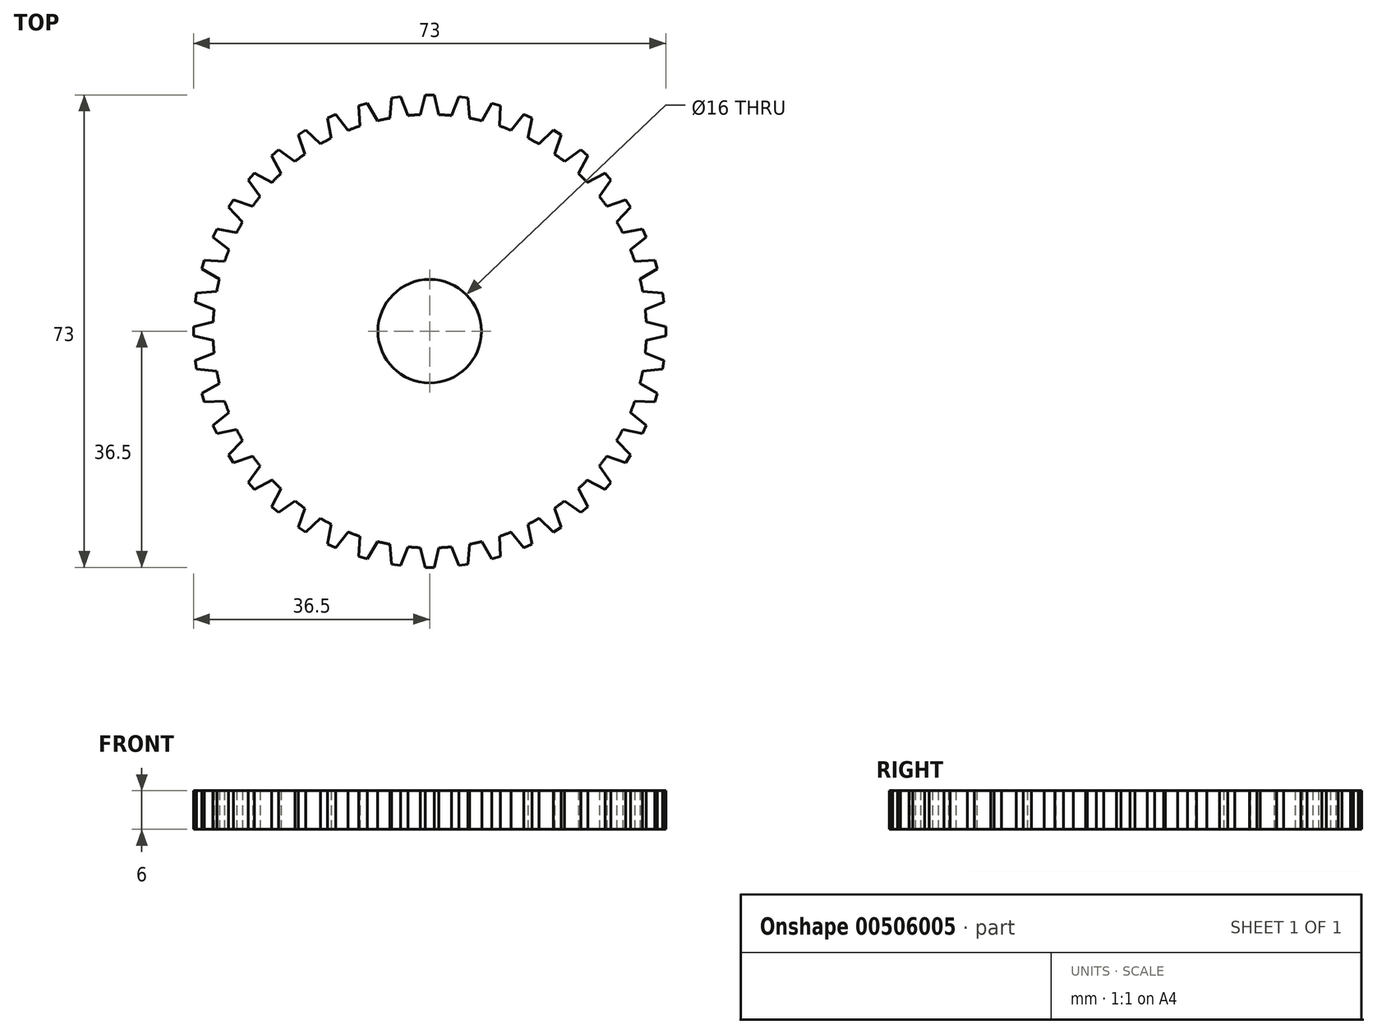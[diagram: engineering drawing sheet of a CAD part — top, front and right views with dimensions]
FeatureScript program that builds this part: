
annotation { "Feature Type Name" : "Feature", "Feature Type Description" : "" }
export const myFeature = defineFeature(function(context is Context, id is Id, definition is map)
    precondition{}
    {
        {
            var Q0;
            Q0=qCreatedBy(makeId("Top.planeOp"),FACE);
            var sketch = newSketch(context, id + "F0", { "sketchPlane" : qUnion([Q0])});
            skPoint(sketch, "E0.center", {"position": v(0, 0) * mm});
            skCircle(sketch, "E1", {"center": v(0, 0) * mm, "radius": 33.5 * mm});
            skLineSegment(sketch, "E2", {"start": v(0, 36.5) * mm, "end": v(0.7, 36.5) * mm});
            skLineSegment(sketch, "E3", {"start": v(0.7, 36.5) * mm, "end": v(1.43, 33.47) * mm});
            skLineSegment(sketch, "E4.MirrorCS", {"start": v(0, 36.5) * mm, "end": v(-0.7, 36.5) * mm});
            skLineSegment(sketch, "E5.MirrorCS", {"start": v(-0.7, 36.5) * mm, "end": v(-1.43, 33.47) * mm});
            skLineSegment(sketch, "E6.1.0", {"start": v(-5.2, 36.13) * mm, "end": v(-4.5, 36.23) * mm});
            skLineSegment(sketch, "E6.1.1", {"start": v(-4.5, 36.23) * mm, "end": v(-3.35, 33.33) * mm});
            skLineSegment(sketch, "E6.1.2", {"start": v(-5.89, 36.03) * mm, "end": v(-6.18, 32.93) * mm});
            skLineSegment(sketch, "E6.1.3", {"start": v(-5.2, 36.13) * mm, "end": v(-5.89, 36.03) * mm});
            skLineSegment(sketch, "E6.2.0", {"start": v(-10.28, 35.02) * mm, "end": v(-9.61, 35.22) * mm});
            skLineSegment(sketch, "E6.2.1", {"start": v(-9.61, 35.22) * mm, "end": v(-8.06, 32.52) * mm});
            skLineSegment(sketch, "E6.2.2", {"start": v(-10.95, 34.82) * mm, "end": v(-10.8, 31.71) * mm});
            skLineSegment(sketch, "E6.2.3", {"start": v(-10.28, 35.02) * mm, "end": v(-10.95, 34.82) * mm});
            skLineSegment(sketch, "E6.3.0", {"start": v(-15.16, 33.2) * mm, "end": v(-14.53, 33.5) * mm});
            skLineSegment(sketch, "E6.3.1", {"start": v(-14.53, 33.5) * mm, "end": v(-12.6, 31.04) * mm});
            skLineSegment(sketch, "E6.3.2", {"start": v(-15.8, 32.91) * mm, "end": v(-15.2, 29.85) * mm});
            skLineSegment(sketch, "E6.3.3", {"start": v(-15.16, 33.2) * mm, "end": v(-15.8, 32.91) * mm});
            skLineSegment(sketch, "E6.4.0", {"start": v(-19.73, 30.7) * mm, "end": v(-19.14, 31.08) * mm});
            skLineSegment(sketch, "E6.4.1", {"start": v(-19.14, 31.08) * mm, "end": v(-16.9, 28.93) * mm});
            skLineSegment(sketch, "E6.4.2", {"start": v(-20.32, 30.33) * mm, "end": v(-19.3, 27.38) * mm});
            skLineSegment(sketch, "E6.4.3", {"start": v(-19.73, 30.7) * mm, "end": v(-20.32, 30.33) * mm});
            skLineSegment(sketch, "E6.5.0", {"start": v(-23.9, 27.58) * mm, "end": v(-23.37, 28.04) * mm});
            skLineSegment(sketch, "E6.5.1", {"start": v(-23.37, 28.04) * mm, "end": v(-20.84, 26.23) * mm});
            skLineSegment(sketch, "E6.5.2", {"start": v(-24.43, 27.13) * mm, "end": v(-23, 24.36) * mm});
            skLineSegment(sketch, "E6.5.3", {"start": v(-23.9, 27.58) * mm, "end": v(-24.43, 27.13) * mm});
            skLineSegment(sketch, "E6.6.0", {"start": v(-27.58, 23.9) * mm, "end": v(-27.13, 24.43) * mm});
            skLineSegment(sketch, "E6.6.1", {"start": v(-27.13, 24.43) * mm, "end": v(-24.36, 23) * mm});
            skLineSegment(sketch, "E6.6.2", {"start": v(-28.04, 23.37) * mm, "end": v(-26.23, 20.84) * mm});
            skLineSegment(sketch, "E6.6.3", {"start": v(-27.58, 23.9) * mm, "end": v(-28.04, 23.37) * mm});
            skLineSegment(sketch, "E6.7.0", {"start": v(-30.7, 19.73) * mm, "end": v(-30.33, 20.32) * mm});
            skLineSegment(sketch, "E6.7.1", {"start": v(-30.33, 20.32) * mm, "end": v(-27.38, 19.3) * mm});
            skLineSegment(sketch, "E6.7.2", {"start": v(-31.08, 19.14) * mm, "end": v(-28.93, 16.9) * mm});
            skLineSegment(sketch, "E6.7.3", {"start": v(-30.7, 19.73) * mm, "end": v(-31.08, 19.14) * mm});
            skLineSegment(sketch, "E6.8.0", {"start": v(-33.2, 15.16) * mm, "end": v(-32.91, 15.8) * mm});
            skLineSegment(sketch, "E6.8.1", {"start": v(-32.91, 15.8) * mm, "end": v(-29.85, 15.2) * mm});
            skLineSegment(sketch, "E6.8.2", {"start": v(-33.5, 14.53) * mm, "end": v(-31.04, 12.6) * mm});
            skLineSegment(sketch, "E6.8.3", {"start": v(-33.2, 15.16) * mm, "end": v(-33.5, 14.53) * mm});
            skLineSegment(sketch, "E6.9.0", {"start": v(-35.02, 10.28) * mm, "end": v(-34.82, 10.95) * mm});
            skLineSegment(sketch, "E6.9.1", {"start": v(-34.82, 10.95) * mm, "end": v(-31.71, 10.8) * mm});
            skLineSegment(sketch, "E6.9.2", {"start": v(-35.22, 9.61) * mm, "end": v(-32.52, 8.06) * mm});
            skLineSegment(sketch, "E6.9.3", {"start": v(-35.02, 10.28) * mm, "end": v(-35.22, 9.61) * mm});
            skLineSegment(sketch, "E6.10.0", {"start": v(-36.13, 5.2) * mm, "end": v(-36.03, 5.89) * mm});
            skLineSegment(sketch, "E6.10.1", {"start": v(-36.03, 5.89) * mm, "end": v(-32.93, 6.18) * mm});
            skLineSegment(sketch, "E6.10.2", {"start": v(-36.23, 4.5) * mm, "end": v(-33.33, 3.35) * mm});
            skLineSegment(sketch, "E6.10.3", {"start": v(-36.13, 5.2) * mm, "end": v(-36.23, 4.5) * mm});
            skLineSegment(sketch, "E6.11.0", {"start": v(-36.5, 0) * mm, "end": v(-36.5, 0.7) * mm});
            skLineSegment(sketch, "E6.11.1", {"start": v(-36.5, 0.7) * mm, "end": v(-33.47, 1.43) * mm});
            skLineSegment(sketch, "E6.11.2", {"start": v(-36.5, -0.7) * mm, "end": v(-33.47, -1.43) * mm});
            skLineSegment(sketch, "E6.11.3", {"start": v(-36.5, 0) * mm, "end": v(-36.5, -0.7) * mm});
            skLineSegment(sketch, "E6.12.0", {"start": v(-36.13, -5.2) * mm, "end": v(-36.23, -4.5) * mm});
            skLineSegment(sketch, "E6.12.1", {"start": v(-36.23, -4.5) * mm, "end": v(-33.33, -3.35) * mm});
            skLineSegment(sketch, "E6.12.2", {"start": v(-36.03, -5.89) * mm, "end": v(-32.93, -6.18) * mm});
            skLineSegment(sketch, "E6.12.3", {"start": v(-36.13, -5.2) * mm, "end": v(-36.03, -5.89) * mm});
            skLineSegment(sketch, "E6.13.0", {"start": v(-35.02, -10.28) * mm, "end": v(-35.22, -9.61) * mm});
            skLineSegment(sketch, "E6.13.1", {"start": v(-35.22, -9.61) * mm, "end": v(-32.52, -8.06) * mm});
            skLineSegment(sketch, "E6.13.2", {"start": v(-34.82, -10.95) * mm, "end": v(-31.71, -10.8) * mm});
            skLineSegment(sketch, "E6.13.3", {"start": v(-35.02, -10.28) * mm, "end": v(-34.82, -10.95) * mm});
            skLineSegment(sketch, "E6.14.0", {"start": v(-33.2, -15.16) * mm, "end": v(-33.5, -14.53) * mm});
            skLineSegment(sketch, "E6.14.1", {"start": v(-33.5, -14.53) * mm, "end": v(-31.04, -12.6) * mm});
            skLineSegment(sketch, "E6.14.2", {"start": v(-32.91, -15.8) * mm, "end": v(-29.85, -15.2) * mm});
            skLineSegment(sketch, "E6.14.3", {"start": v(-33.2, -15.16) * mm, "end": v(-32.91, -15.8) * mm});
            skLineSegment(sketch, "E6.15.0", {"start": v(-30.7, -19.73) * mm, "end": v(-31.08, -19.14) * mm});
            skLineSegment(sketch, "E6.15.1", {"start": v(-31.08, -19.14) * mm, "end": v(-28.93, -16.9) * mm});
            skLineSegment(sketch, "E6.15.2", {"start": v(-30.33, -20.32) * mm, "end": v(-27.38, -19.3) * mm});
            skLineSegment(sketch, "E6.15.3", {"start": v(-30.7, -19.73) * mm, "end": v(-30.33, -20.32) * mm});
            skLineSegment(sketch, "E6.16.0", {"start": v(-27.58, -23.9) * mm, "end": v(-28.04, -23.37) * mm});
            skLineSegment(sketch, "E6.16.1", {"start": v(-28.04, -23.37) * mm, "end": v(-26.23, -20.84) * mm});
            skLineSegment(sketch, "E6.16.2", {"start": v(-27.13, -24.43) * mm, "end": v(-24.36, -23) * mm});
            skLineSegment(sketch, "E6.16.3", {"start": v(-27.58, -23.9) * mm, "end": v(-27.13, -24.43) * mm});
            skLineSegment(sketch, "E6.17.0", {"start": v(-23.9, -27.58) * mm, "end": v(-24.43, -27.13) * mm});
            skLineSegment(sketch, "E6.17.1", {"start": v(-24.43, -27.13) * mm, "end": v(-23, -24.36) * mm});
            skLineSegment(sketch, "E6.17.2", {"start": v(-23.37, -28.04) * mm, "end": v(-20.84, -26.23) * mm});
            skLineSegment(sketch, "E6.17.3", {"start": v(-23.9, -27.58) * mm, "end": v(-23.37, -28.04) * mm});
            skLineSegment(sketch, "E6.18.0", {"start": v(-19.73, -30.7) * mm, "end": v(-20.32, -30.33) * mm});
            skLineSegment(sketch, "E6.18.1", {"start": v(-20.32, -30.33) * mm, "end": v(-19.3, -27.38) * mm});
            skLineSegment(sketch, "E6.18.2", {"start": v(-19.14, -31.08) * mm, "end": v(-16.9, -28.93) * mm});
            skLineSegment(sketch, "E6.18.3", {"start": v(-19.73, -30.7) * mm, "end": v(-19.14, -31.08) * mm});
            skLineSegment(sketch, "E6.19.0", {"start": v(-15.16, -33.2) * mm, "end": v(-15.8, -32.91) * mm});
            skLineSegment(sketch, "E6.19.1", {"start": v(-15.8, -32.91) * mm, "end": v(-15.2, -29.85) * mm});
            skLineSegment(sketch, "E6.19.2", {"start": v(-14.53, -33.5) * mm, "end": v(-12.6, -31.04) * mm});
            skLineSegment(sketch, "E6.19.3", {"start": v(-15.16, -33.2) * mm, "end": v(-14.53, -33.5) * mm});
            skLineSegment(sketch, "E6.20.0", {"start": v(-10.28, -35.02) * mm, "end": v(-10.95, -34.82) * mm});
            skLineSegment(sketch, "E6.20.1", {"start": v(-10.95, -34.82) * mm, "end": v(-10.8, -31.71) * mm});
            skLineSegment(sketch, "E6.20.2", {"start": v(-9.61, -35.22) * mm, "end": v(-8.06, -32.52) * mm});
            skLineSegment(sketch, "E6.20.3", {"start": v(-10.28, -35.02) * mm, "end": v(-9.61, -35.22) * mm});
            skLineSegment(sketch, "E6.21.0", {"start": v(-5.2, -36.13) * mm, "end": v(-5.89, -36.03) * mm});
            skLineSegment(sketch, "E6.21.1", {"start": v(-5.89, -36.03) * mm, "end": v(-6.18, -32.93) * mm});
            skLineSegment(sketch, "E6.21.2", {"start": v(-4.5, -36.23) * mm, "end": v(-3.35, -33.33) * mm});
            skLineSegment(sketch, "E6.21.3", {"start": v(-5.2, -36.13) * mm, "end": v(-4.5, -36.23) * mm});
            skLineSegment(sketch, "E6.22.0", {"start": v(0, -36.5) * mm, "end": v(-0.7, -36.5) * mm});
            skLineSegment(sketch, "E6.22.1", {"start": v(-0.7, -36.5) * mm, "end": v(-1.43, -33.47) * mm});
            skLineSegment(sketch, "E6.22.2", {"start": v(0.7, -36.5) * mm, "end": v(1.43, -33.47) * mm});
            skLineSegment(sketch, "E6.22.3", {"start": v(0, -36.5) * mm, "end": v(0.7, -36.5) * mm});
            skLineSegment(sketch, "E6.23.0", {"start": v(5.2, -36.13) * mm, "end": v(4.5, -36.23) * mm});
            skLineSegment(sketch, "E6.23.1", {"start": v(4.5, -36.23) * mm, "end": v(3.35, -33.33) * mm});
            skLineSegment(sketch, "E6.23.2", {"start": v(5.89, -36.03) * mm, "end": v(6.18, -32.93) * mm});
            skLineSegment(sketch, "E6.23.3", {"start": v(5.2, -36.13) * mm, "end": v(5.89, -36.03) * mm});
            skLineSegment(sketch, "E6.24.0", {"start": v(10.28, -35.02) * mm, "end": v(9.61, -35.22) * mm});
            skLineSegment(sketch, "E6.24.1", {"start": v(9.61, -35.22) * mm, "end": v(8.06, -32.52) * mm});
            skLineSegment(sketch, "E6.24.2", {"start": v(10.95, -34.82) * mm, "end": v(10.8, -31.71) * mm});
            skLineSegment(sketch, "E6.24.3", {"start": v(10.28, -35.02) * mm, "end": v(10.95, -34.82) * mm});
            skLineSegment(sketch, "E6.25.0", {"start": v(15.16, -33.2) * mm, "end": v(14.53, -33.5) * mm});
            skLineSegment(sketch, "E6.25.1", {"start": v(14.53, -33.5) * mm, "end": v(12.6, -31.04) * mm});
            skLineSegment(sketch, "E6.25.2", {"start": v(15.8, -32.91) * mm, "end": v(15.2, -29.85) * mm});
            skLineSegment(sketch, "E6.25.3", {"start": v(15.16, -33.2) * mm, "end": v(15.8, -32.91) * mm});
            skLineSegment(sketch, "E6.26.0", {"start": v(19.73, -30.7) * mm, "end": v(19.14, -31.08) * mm});
            skLineSegment(sketch, "E6.26.1", {"start": v(19.14, -31.08) * mm, "end": v(16.9, -28.93) * mm});
            skLineSegment(sketch, "E6.26.2", {"start": v(20.32, -30.33) * mm, "end": v(19.3, -27.38) * mm});
            skLineSegment(sketch, "E6.26.3", {"start": v(19.73, -30.7) * mm, "end": v(20.32, -30.33) * mm});
            skLineSegment(sketch, "E6.27.0", {"start": v(23.9, -27.58) * mm, "end": v(23.37, -28.04) * mm});
            skLineSegment(sketch, "E6.27.1", {"start": v(23.37, -28.04) * mm, "end": v(20.84, -26.23) * mm});
            skLineSegment(sketch, "E6.27.2", {"start": v(24.43, -27.13) * mm, "end": v(23, -24.36) * mm});
            skLineSegment(sketch, "E6.27.3", {"start": v(23.9, -27.58) * mm, "end": v(24.43, -27.13) * mm});
            skLineSegment(sketch, "E6.28.0", {"start": v(27.58, -23.9) * mm, "end": v(27.13, -24.43) * mm});
            skLineSegment(sketch, "E6.28.1", {"start": v(27.13, -24.43) * mm, "end": v(24.36, -23) * mm});
            skLineSegment(sketch, "E6.28.2", {"start": v(28.04, -23.37) * mm, "end": v(26.23, -20.84) * mm});
            skLineSegment(sketch, "E6.28.3", {"start": v(27.58, -23.9) * mm, "end": v(28.04, -23.37) * mm});
            skLineSegment(sketch, "E6.29.0", {"start": v(30.7, -19.73) * mm, "end": v(30.33, -20.32) * mm});
            skLineSegment(sketch, "E6.29.1", {"start": v(30.33, -20.32) * mm, "end": v(27.38, -19.3) * mm});
            skLineSegment(sketch, "E6.29.2", {"start": v(31.08, -19.14) * mm, "end": v(28.93, -16.9) * mm});
            skLineSegment(sketch, "E6.29.3", {"start": v(30.7, -19.73) * mm, "end": v(31.08, -19.14) * mm});
            skLineSegment(sketch, "E6.30.0", {"start": v(33.2, -15.16) * mm, "end": v(32.91, -15.8) * mm});
            skLineSegment(sketch, "E6.30.1", {"start": v(32.91, -15.8) * mm, "end": v(29.85, -15.2) * mm});
            skLineSegment(sketch, "E6.30.2", {"start": v(33.5, -14.53) * mm, "end": v(31.04, -12.6) * mm});
            skLineSegment(sketch, "E6.30.3", {"start": v(33.2, -15.16) * mm, "end": v(33.5, -14.53) * mm});
            skLineSegment(sketch, "E6.31.0", {"start": v(35.02, -10.28) * mm, "end": v(34.82, -10.95) * mm});
            skLineSegment(sketch, "E6.31.1", {"start": v(34.82, -10.95) * mm, "end": v(31.71, -10.8) * mm});
            skLineSegment(sketch, "E6.31.2", {"start": v(35.22, -9.61) * mm, "end": v(32.52, -8.06) * mm});
            skLineSegment(sketch, "E6.31.3", {"start": v(35.02, -10.28) * mm, "end": v(35.22, -9.61) * mm});
            skLineSegment(sketch, "E6.32.0", {"start": v(36.13, -5.2) * mm, "end": v(36.03, -5.89) * mm});
            skLineSegment(sketch, "E6.32.1", {"start": v(36.03, -5.89) * mm, "end": v(32.93, -6.18) * mm});
            skLineSegment(sketch, "E6.32.2", {"start": v(36.23, -4.5) * mm, "end": v(33.33, -3.35) * mm});
            skLineSegment(sketch, "E6.32.3", {"start": v(36.13, -5.2) * mm, "end": v(36.23, -4.5) * mm});
            skLineSegment(sketch, "E6.33.0", {"start": v(36.5, 0) * mm, "end": v(36.5, -0.7) * mm});
            skLineSegment(sketch, "E6.33.1", {"start": v(36.5, -0.7) * mm, "end": v(33.47, -1.43) * mm});
            skLineSegment(sketch, "E6.33.2", {"start": v(36.5, 0.7) * mm, "end": v(33.47, 1.43) * mm});
            skLineSegment(sketch, "E6.33.3", {"start": v(36.5, 0) * mm, "end": v(36.5, 0.7) * mm});
            skLineSegment(sketch, "E6.34.0", {"start": v(36.13, 5.2) * mm, "end": v(36.23, 4.5) * mm});
            skLineSegment(sketch, "E6.34.1", {"start": v(36.23, 4.5) * mm, "end": v(33.33, 3.35) * mm});
            skLineSegment(sketch, "E6.34.2", {"start": v(36.03, 5.89) * mm, "end": v(32.93, 6.18) * mm});
            skLineSegment(sketch, "E6.34.3", {"start": v(36.13, 5.2) * mm, "end": v(36.03, 5.89) * mm});
            skLineSegment(sketch, "E6.35.0", {"start": v(35.02, 10.28) * mm, "end": v(35.22, 9.61) * mm});
            skLineSegment(sketch, "E6.35.1", {"start": v(35.22, 9.61) * mm, "end": v(32.52, 8.06) * mm});
            skLineSegment(sketch, "E6.35.2", {"start": v(34.82, 10.95) * mm, "end": v(31.71, 10.8) * mm});
            skLineSegment(sketch, "E6.35.3", {"start": v(35.02, 10.28) * mm, "end": v(34.82, 10.95) * mm});
            skLineSegment(sketch, "E6.36.0", {"start": v(33.2, 15.16) * mm, "end": v(33.5, 14.53) * mm});
            skLineSegment(sketch, "E6.36.1", {"start": v(33.5, 14.53) * mm, "end": v(31.04, 12.6) * mm});
            skLineSegment(sketch, "E6.36.2", {"start": v(32.91, 15.8) * mm, "end": v(29.85, 15.2) * mm});
            skLineSegment(sketch, "E6.36.3", {"start": v(33.2, 15.16) * mm, "end": v(32.91, 15.8) * mm});
            skLineSegment(sketch, "E6.37.0", {"start": v(30.7, 19.73) * mm, "end": v(31.08, 19.14) * mm});
            skLineSegment(sketch, "E6.37.1", {"start": v(31.08, 19.14) * mm, "end": v(28.93, 16.9) * mm});
            skLineSegment(sketch, "E6.37.2", {"start": v(30.33, 20.32) * mm, "end": v(27.38, 19.3) * mm});
            skLineSegment(sketch, "E6.37.3", {"start": v(30.7, 19.73) * mm, "end": v(30.33, 20.32) * mm});
            skLineSegment(sketch, "E6.38.0", {"start": v(27.58, 23.9) * mm, "end": v(28.04, 23.37) * mm});
            skLineSegment(sketch, "E6.38.1", {"start": v(28.04, 23.37) * mm, "end": v(26.23, 20.84) * mm});
            skLineSegment(sketch, "E6.38.2", {"start": v(27.13, 24.43) * mm, "end": v(24.36, 23) * mm});
            skLineSegment(sketch, "E6.38.3", {"start": v(27.58, 23.9) * mm, "end": v(27.13, 24.43) * mm});
            skLineSegment(sketch, "E6.39.0", {"start": v(23.9, 27.58) * mm, "end": v(24.43, 27.13) * mm});
            skLineSegment(sketch, "E6.39.1", {"start": v(24.43, 27.13) * mm, "end": v(23, 24.36) * mm});
            skLineSegment(sketch, "E6.39.2", {"start": v(23.37, 28.04) * mm, "end": v(20.84, 26.23) * mm});
            skLineSegment(sketch, "E6.39.3", {"start": v(23.9, 27.58) * mm, "end": v(23.37, 28.04) * mm});
            skLineSegment(sketch, "E6.40.0", {"start": v(19.73, 30.7) * mm, "end": v(20.32, 30.33) * mm});
            skLineSegment(sketch, "E6.40.1", {"start": v(20.32, 30.33) * mm, "end": v(19.3, 27.38) * mm});
            skLineSegment(sketch, "E6.40.2", {"start": v(19.14, 31.08) * mm, "end": v(16.9, 28.93) * mm});
            skLineSegment(sketch, "E6.40.3", {"start": v(19.73, 30.7) * mm, "end": v(19.14, 31.08) * mm});
            skLineSegment(sketch, "E6.41.0", {"start": v(15.16, 33.2) * mm, "end": v(15.8, 32.91) * mm});
            skLineSegment(sketch, "E6.41.1", {"start": v(15.8, 32.91) * mm, "end": v(15.2, 29.85) * mm});
            skLineSegment(sketch, "E6.41.2", {"start": v(14.53, 33.5) * mm, "end": v(12.6, 31.04) * mm});
            skLineSegment(sketch, "E6.41.3", {"start": v(15.16, 33.2) * mm, "end": v(14.53, 33.5) * mm});
            skLineSegment(sketch, "E6.42.0", {"start": v(10.28, 35.02) * mm, "end": v(10.95, 34.82) * mm});
            skLineSegment(sketch, "E6.42.1", {"start": v(10.95, 34.82) * mm, "end": v(10.8, 31.71) * mm});
            skLineSegment(sketch, "E6.42.2", {"start": v(9.61, 35.22) * mm, "end": v(8.06, 32.52) * mm});
            skLineSegment(sketch, "E6.42.3", {"start": v(10.28, 35.02) * mm, "end": v(9.61, 35.22) * mm});
            skLineSegment(sketch, "E6.43.0", {"start": v(5.2, 36.13) * mm, "end": v(5.89, 36.03) * mm});
            skLineSegment(sketch, "E6.43.1", {"start": v(5.89, 36.03) * mm, "end": v(6.18, 32.93) * mm});
            skLineSegment(sketch, "E6.43.2", {"start": v(4.5, 36.23) * mm, "end": v(3.35, 33.33) * mm});
            skLineSegment(sketch, "E6.43.3", {"start": v(5.2, 36.13) * mm, "end": v(4.5, 36.23) * mm});
            skCircle(sketch, "E7", {"center": v(0, 0) * mm, "radius": 8 * mm});
            skSolve(sketch);
        }
        {
            var Q0;
            Q0 = qSketchRegion(id + "F0", true);
            extrude(context, id + "F1", {"entities" : qUnion([Q0]), "depth" : 6 * mm, "offsetDistance" : 25 * mm});
        }
    });
